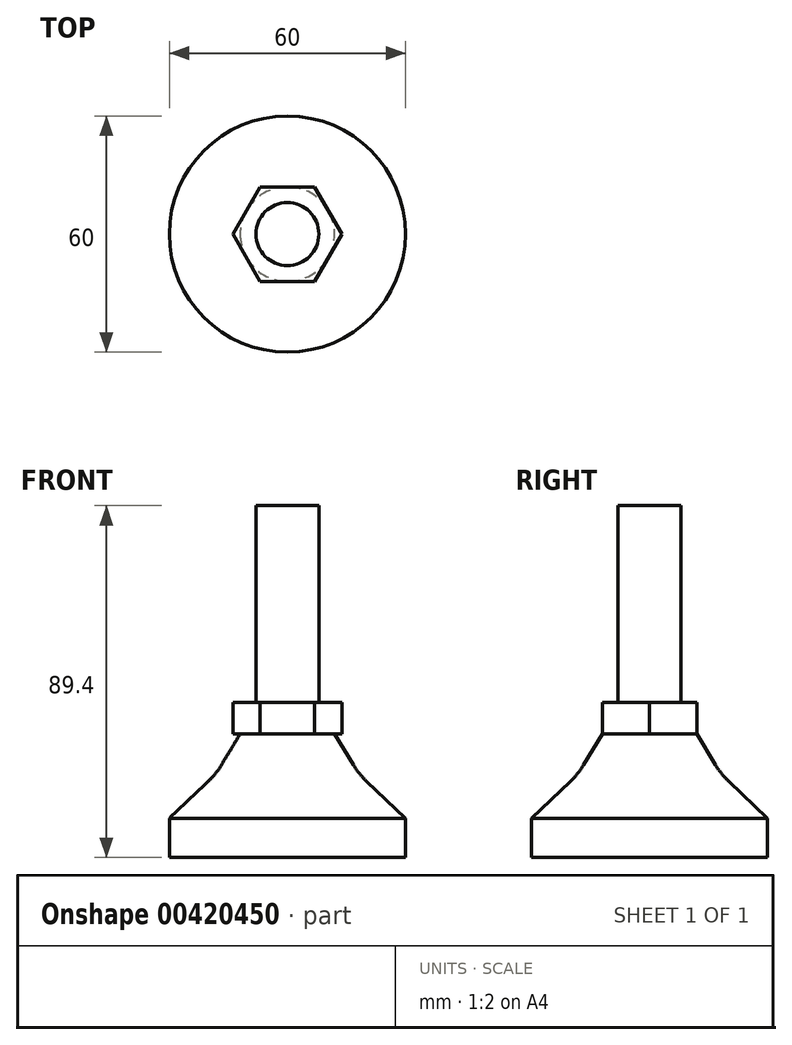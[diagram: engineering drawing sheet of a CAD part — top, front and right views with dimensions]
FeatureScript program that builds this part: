
annotation { "Feature Type Name" : "Feature", "Feature Type Description" : "" }
export const myFeature = defineFeature(function(context is Context, id is Id, definition is map)
    precondition{}
    {
        {
            var Q0;
            Q0=qCreatedBy(makeId("Top.planeOp"),FACE);
            var sketch = newSketch(context, id + "F0", { "sketchPlane" : qUnion([Q0])});
            skCircle(sketch, "E0", {"center": v(0, 0) * mm, "radius": 30 * mm});
            skSolve(sketch);
        }
        {
            var Q0;
            Q0 = qSketchRegion(id + "F0", true);
            extrude(context, id + "F1", {"entities" : qUnion([Q0]), "depth" : 10 * mm});
        }
        {
            var Q0;
            Q0=qCreatedBy(makeId("Front.planeOp"),FACE);
            var sketch = newSketch(context, id + "F2", { "sketchPlane" : qUnion([Q0])});
            skLineSegment(sketch, "E1", {"start": v(0, 10) * mm, "end": v(0, 31.4) * mm});
            skLineSegment(sketch, "E2", {"start": v(-30, 10) * mm, "end": v(0, 10) * mm});
            skLineSegment(sketch, "E3", {"start": v(-12, 31.4) * mm, "end": v(0, 31.4) * mm});
            skLineSegment(sketch, "E4", {"start": v(0, -16) * mm, "end": v(0, 55.68) * mm, "construction": true});
            skLineSegment(sketch, "E5", {"start": v(-12, 31.4) * mm, "end": v(-16.79, 23.49) * mm});
            skLineSegment(sketch, "E6", {"start": v(-20.15, 19.32) * mm, "end": v(-30, 10) * mm});
            skPoint(sketch, "E7.visualSharp", {"position": v(-18.19, 21.18) * mm});
            skArc(sketch, "E7.filletArc", {"start": v(-20.15, 19.32) * mm, "mid": v(-18.33, 21.3) * mm, "end": v(-16.79, 23.49) * mm});
            skSolve(sketch);
        }
        {
            var Q0;
            Q0 = qSketchRegion(id + "F2", true);
            var Q1;
            Q1=makeQuery(id+"F1.opExtrude","CAP_EDGE",EDGE,{"disambiguationData":[OSD([sQuery(id+"F0.wireOp",EDGE,"E0")])],"isStart":false});
            sweep(context, id + "F3", {"operationType" : NewBodyOperationType.ADD, "profiles" : qUnion([Q0]), "path" : qUnion([Q1])});
        }
        {
            var Q0;
            Q0=makeQuery(id+"F3.opSweep","SWEPT_FACE",FACE,{"disambiguationData":[OSD([sQuery(id+"F0.wireOp",EDGE,"E0"),sQuery(id+"F2.wireOp",EDGE,"E3")])]});
            var sketch = newSketch(context, id + "F4", { "sketchPlane" : qUnion([Q0])});
            skCircle(sketch, "E8.cCircle", {"center": v(0, 0) * mm, "radius": 12 * mm, "construction": true});
            skLineSegment(sketch, "E8.0", {"start": v(-6.93, 12) * mm, "end": v(6.93, 12) * mm});
            skLineSegment(sketch, "E8.1", {"start": v(6.93, 12) * mm, "end": v(13.86, 0) * mm});
            skLineSegment(sketch, "E8.2", {"start": v(13.86, 0) * mm, "end": v(6.93, -12) * mm});
            skLineSegment(sketch, "E8.3", {"start": v(6.93, -12) * mm, "end": v(-6.93, -12) * mm});
            skLineSegment(sketch, "E8.4", {"start": v(-6.93, -12) * mm, "end": v(-13.86, 0) * mm});
            skLineSegment(sketch, "E8.5", {"start": v(-13.86, 0) * mm, "end": v(-6.93, 12) * mm});
            skPoint(sketch, "E8.0.midPoint", {"position": v(0, 12) * mm});
            skSolve(sketch);
        }
        {
            var Q0;
            Q0 = qSketchRegion(id + "F4", true);
            extrude(context, id + "F5", {"entities" : qUnion([Q0]), "operationType" : NewBodyOperationType.ADD, "depth" : 8 * mm});
        }
        {
            var Q0;
            Q0=makeQuery(id+"F5.opExtrude","CAP_FACE",FACE,{"disambiguationData":[OSD([sQuery(id+"F4.wireOp",EDGE,"E8.0"),sQuery(id+"F4.wireOp",EDGE,"E8.1"),sQuery(id+"F4.wireOp",EDGE,"E8.2"),sQuery(id+"F4.wireOp",EDGE,"E8.3"),sQuery(id+"F4.wireOp",EDGE,"E8.4"),sQuery(id+"F4.wireOp",EDGE,"E8.5")])],"isStart":false});
            var sketch = newSketch(context, id + "F6", { "sketchPlane" : qUnion([Q0])});
            skCircle(sketch, "E9", {"center": v(0, 0) * mm, "radius": 8 * mm});
            skSolve(sketch);
        }
        {
            var Q0;
            Q0 = qSketchRegion(id + "F6", true);
            extrude(context, id + "F7", {"entities" : qUnion([Q0]), "operationType" : NewBodyOperationType.ADD, "depth" : 50 * mm});
        }
    });
